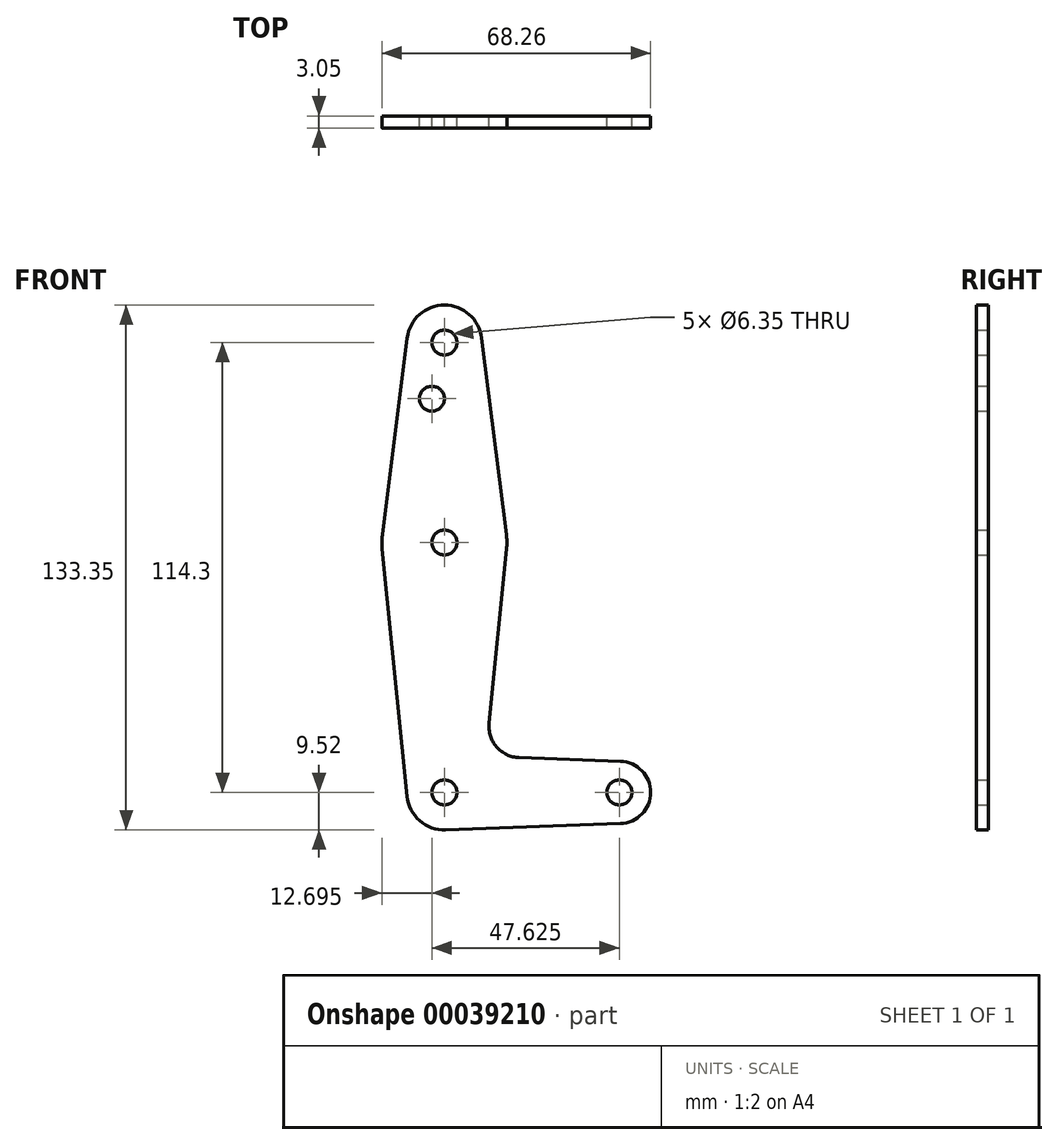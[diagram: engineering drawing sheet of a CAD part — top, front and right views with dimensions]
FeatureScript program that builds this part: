
annotation { "Feature Type Name" : "Feature", "Feature Type Description" : "" }
export const myFeature = defineFeature(function(context is Context, id is Id, definition is map)
    precondition{}
    {
        {
            var Q0;
            Q0=qCreatedBy(makeId("Front.planeOp"),FACE);
            var sketch = newSketch(context, id + "F0", { "sketchPlane" : qUnion([Q0])});
            skCircle(sketch, "E0", {"center": v(0, 0) * mm, "radius": 9.53 * mm});
            skCircle(sketch, "E1", {"center": v(0, 63.5) * mm, "radius": 15.88 * mm});
            skCircle(sketch, "E2", {"center": v(0, 114.3) * mm, "radius": 9.53 * mm});
            skCircle(sketch, "E3", {"center": v(44.45, 0) * mm, "radius": 7.94 * mm});
            skLineSegment(sketch, "E4", {"start": v(0, 0) * mm, "end": v(0, 114.3) * mm, "construction": true});
            skLineSegment(sketch, "E5", {"start": v(0, 0) * mm, "end": v(44.45, 0) * mm, "construction": true});
            skLineSegment(sketch, "E6", {"start": v(15.8, 61.91) * mm, "end": v(11.34, 17.6) * mm});
            skLineSegment(sketch, "E7", {"start": v(-9.45, 115.5) * mm, "end": v(-15.75, 65.48) * mm});
            skLineSegment(sketch, "E8", {"start": v(9.45, 115.5) * mm, "end": v(15.75, 65.48) * mm});
            skLineSegment(sketch, "E9", {"start": v(-15.8, 61.91) * mm, "end": v(-9.48, -0.95) * mm});
            skLineSegment(sketch, "E10", {"start": v(0.34, -9.52) * mm, "end": v(44.73, -7.93) * mm});
            skLineSegment(sketch, "E11", {"start": v(18.97, 8.85) * mm, "end": v(44.73, 7.93) * mm});
            skPoint(sketch, "E12.newPointA", {"position": v(0, 9.53) * mm});
            skArc(sketch, "E12.filletArc", {"start": v(11.34, 17.6) * mm, "mid": v(13.26, 11.57) * mm, "end": v(18.97, 8.85) * mm});
            skCircle(sketch, "E13", {"center": v(0, 114.3) * mm, "radius": 3.18 * mm});
            skCircle(sketch, "E14", {"center": v(0, 63.5) * mm, "radius": 3.18 * mm});
            skCircle(sketch, "E15", {"center": v(0, 0) * mm, "radius": 0.83 * mm});
            skCircle(sketch, "E16", {"center": v(44.45, 0) * mm, "radius": 3.18 * mm});
            skCircle(sketch, "E17", {"center": v(0, 0) * mm, "radius": 3.18 * mm});
            skCircle(sketch, "E18", {"center": v(-3.18, 100.03) * mm, "radius": 3.18 * mm});
            skSolve(sketch);
        }
        {
            var Q0;
            Q0 = qSketchRegion(id + "F0", true);
            extrude(context, id + "F1", {"entities" : qUnion([Q0]), "depth" : 3.05 * mm});
        }
    });
